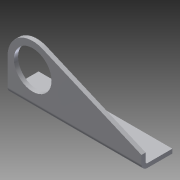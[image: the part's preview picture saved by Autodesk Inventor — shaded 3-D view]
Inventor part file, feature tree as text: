
AUTODESK INVENTOR PART (.ipt)
format: ipt  version: 2014 SP1 (Build 180222100, 222)  size: 184,832 bytes
history: native  units: in
note: dims shown in document units (in); Inventor stores cm internally (conversion verified against a paired STEP export)
features: other x6, sketch x4, sheet_metal_op x3, reference x2, mirror x1
ambient origin geometry x8: Origin, YZ Plane, XZ Plane, XY Plane, X Axis, Y Axis, Z Axis, Center Point
bodies: Solid2 (feature_tree)
feature tree (16):
  sheet_metal_op  "Face2"
  sheet_metal_op  "Flange2"
  mirror  "Mirror1"
  sketch  "Sketch1"  dims[d2=4.0in]
  other  "Plate2"
  sketch  "Sketch5"  dims[d18=0.125in]
  other  "Plate4"
  sheet_metal_op  "Bend2"
  sketch  "Sketch6"  dims[d19=0.125in]
  sketch  "Sketch9"  dims[d40=0.125in d41=0.0625in d42=0.25in d43=0.125in d44=1.75in d45=90.0deg d46=0.05in d47=0.5in d48=0.125in d49=0.125in d50=1.125in d51=0.75in d52=0.75in d53=0.25in d54=0.125in d55=0.0in d57=0.75in d66=0.125in d67=0.0in d0=0.125in d1=0.125in d3=0.125in d4=0.125in d5=0.25in d6=0.125in d7=0.0in]
  reference  "Reference2"
  reference  "Reference3"
  other  "Cut3"
  other  "Cut4"
  other  "Definition1"
  other  "Cut1"
